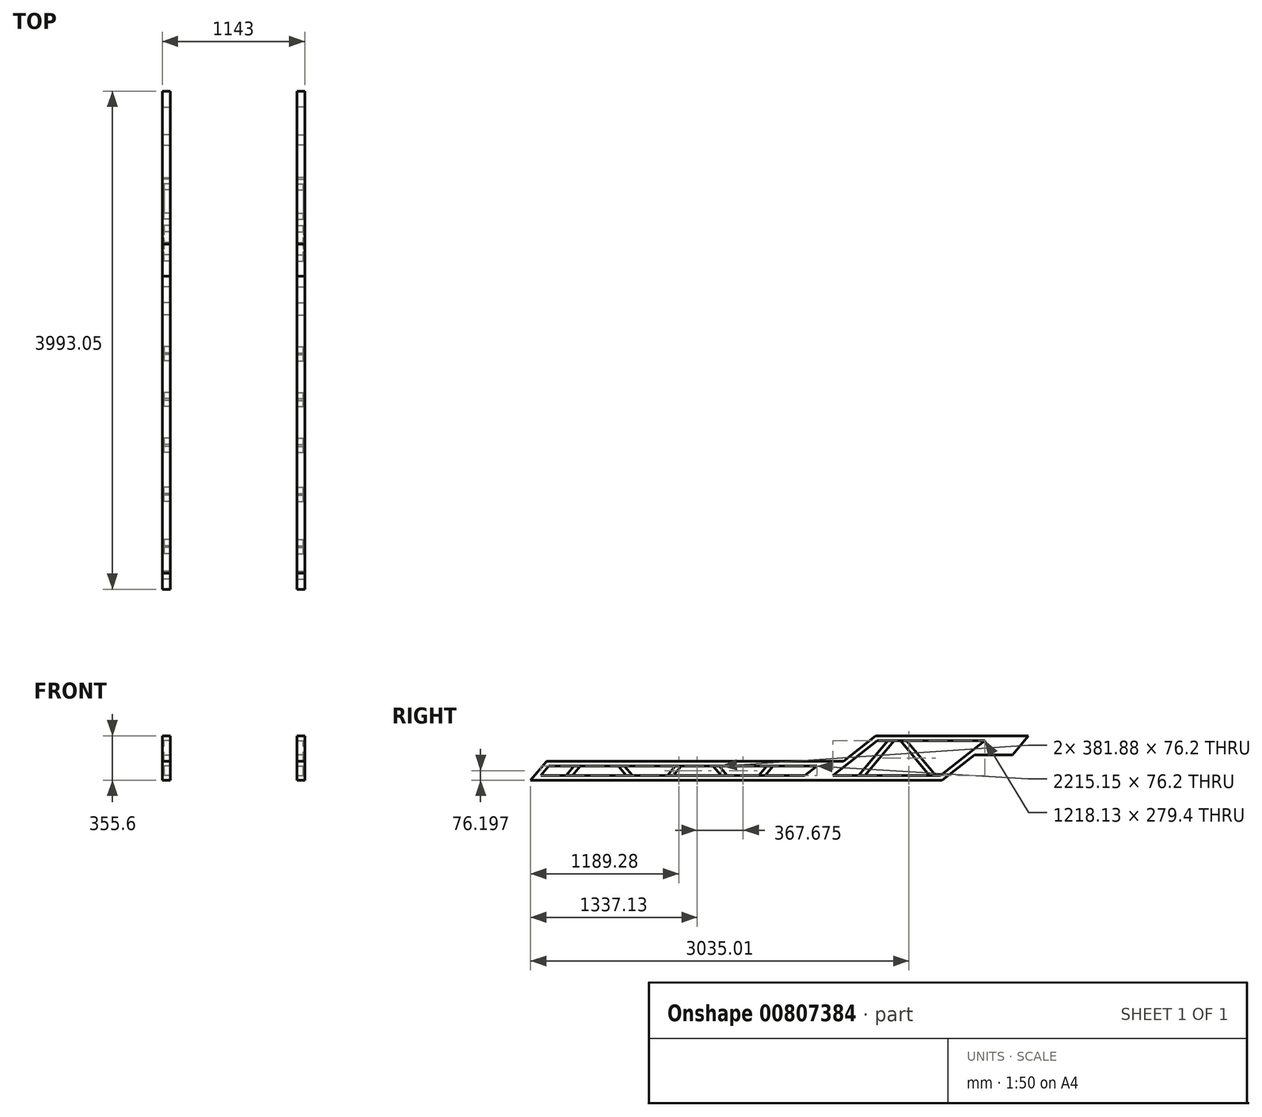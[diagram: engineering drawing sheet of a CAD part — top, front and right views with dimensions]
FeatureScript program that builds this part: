
annotation { "Feature Type Name" : "Feature", "Feature Type Description" : "" }
export const myFeature = defineFeature(function(context is Context, id is Id, definition is map)
    precondition{}
    {
        {
            var Q0;
            Q0=qCreatedBy(makeId("Right.planeOp"),FACE);
            var sketch = newSketch(context, id + "F0", { "sketchPlane" : qUnion([Q0])});
            skLineSegment(sketch, "E0", {"start": v(-1690.82, 358.4) * mm, "end": v(1611.18, 358.4) * mm});
            skLineSegment(sketch, "E1", {"start": v(-1690.82, 358.4) * mm, "end": v(-1562.95, 510.8) * mm});
            skLineSegment(sketch, "E2", {"start": v(-1562.95, 510.8) * mm, "end": v(818.83, 510.8) * mm});
            skLineSegment(sketch, "E3", {"start": v(818.83, 510.8) * mm, "end": v(1077.21, 714) * mm});
            skLineSegment(sketch, "E4", {"start": v(1077.21, 714) * mm, "end": v(2302.23, 714) * mm});
            skLineSegment(sketch, "E5", {"start": v(2302.23, 714) * mm, "end": v(2174.35, 561.6) * mm});
            skLineSegment(sketch, "E6", {"start": v(2174.35, 561.6) * mm, "end": v(1869.55, 561.6) * mm});
            skLineSegment(sketch, "E7", {"start": v(1869.55, 561.6) * mm, "end": v(1611.18, 358.4) * mm});
            skSolve(sketch);
        }
        {
            var Q0;
            Q0=makeQuery(id+"F0.imprint","IMPRINT",FACE,{"disambiguationData":[TD([[makeQuery(id+"F0.imprint","IMPRINT",EDGE,{"derivedFrom":sQuery(id+"F0.wireOp",EDGE,"E0")}),1.0]])]});
            extrude(context, id + "F1", {"entities" : qUnion([Q0]), "depth" : 63.5 * mm, "offsetDistance" : 25.4 * mm});
        }
        {
            var Q0;
            Q0=makeQuery(id+"F1.opExtrude","CAP_FACE",FACE,{"disambiguationData":[OSD([sQuery(id+"F0.wireOp",EDGE,"E0"),sQuery(id+"F0.wireOp",EDGE,"E1"),sQuery(id+"F0.wireOp",EDGE,"E2"),sQuery(id+"F0.wireOp",EDGE,"E3"),sQuery(id+"F0.wireOp",EDGE,"E4"),sQuery(id+"F0.wireOp",EDGE,"E5"),sQuery(id+"F0.wireOp",EDGE,"E6"),sQuery(id+"F0.wireOp",EDGE,"E7")])],"isStart":false});
            var sketch = newSketch(context, id + "F2", { "sketchPlane" : qUnion([Q0])});
            skLineSegment(sketch, "E8.0", {"start": v(832.02, 472.7) * mm, "end": v(1090.4, 675.9) * mm});
            skLineSegment(sketch, "E8.1", {"start": v(-1545.18, 472.7) * mm, "end": v(606.03, 472.7) * mm});
            skLineSegment(sketch, "E8.2", {"start": v(1090.4, 675.9) * mm, "end": v(1953.26, 675.9) * mm});
            skLineSegment(sketch, "E8.3", {"start": v(-1609.12, 396.5) * mm, "end": v(-1545.18, 472.7) * mm});
            skLineSegment(sketch, "E8.7", {"start": v(-1609.12, 396.5) * mm, "end": v(509.14, 396.5) * mm});
            skLineSegment(sketch, "E9", {"start": v(832.02, 472.7) * mm, "end": v(735.13, 396.5) * mm});
            skLineSegment(sketch, "E10", {"start": v(606.03, 472.7) * mm, "end": v(509.14, 396.5) * mm});
            skLineSegment(sketch, "E11.trimOffspring", {"start": v(735.13, 396.5) * mm, "end": v(1597.99, 396.5) * mm});
            skLineSegment(sketch, "E12", {"start": v(1597.99, 396.5) * mm, "end": v(1953.26, 675.9) * mm});
            skSolve(sketch);
        }
        {
            var Q0;
            Q0=makeQuery(id+"F2.imprint","IMPRINT",FACE,{"disambiguationData":[TD([[makeQuery(id+"F2.imprint","IMPRINT",EDGE,{"derivedFrom":sQuery(id+"F2.wireOp",EDGE,"E8.0")}),-1.0]])]});
            var Q1;
            Q1=makeQuery(id+"F2.imprint","IMPRINT",FACE,{"disambiguationData":[TD([[makeQuery(id+"F2.imprint","IMPRINT",EDGE,{"derivedFrom":sQuery(id+"F2.wireOp",EDGE,"E8.1")}),-1.0]])]});
            extrude(context, id + "F3", {"entities" : qUnion([Q0, Q1]), "operationType" : NewBodyOperationType.REMOVE, "oppositeDirection" : true, "depth" : 12.7 * mm, "offsetDistance" : 25.4 * mm});
        }
        {
            var Q0;
            Q0=makeQuery(id+"F3.boolean.opBoolean","COPY",FACE,{"derivedFrom":makeQuery(id+"F3.opExtrude","CAP_FACE",FACE,{"disambiguationData":[OSD([sQuery(id+"F2.wireOp",EDGE,"E8.0"),sQuery(id+"F2.wireOp",EDGE,"E8.1"),sQuery(id+"F2.wireOp",EDGE,"E8.2"),sQuery(id+"F2.wireOp",EDGE,"E8.3"),sQuery(id+"F2.wireOp",EDGE,"E8.4"),sQuery(id+"F2.wireOp",EDGE,"E8.5"),sQuery(id+"F2.wireOp",EDGE,"E8.6"),sQuery(id+"F2.wireOp",EDGE,"E8.7")])],"isStart":false})});
            var sketch = newSketch(context, id + "F4", { "sketchPlane" : qUnion([Q0])});
            skLineSegment(sketch, "E13", {"start": v(-1545.18, 472.7) * mm, "end": v(-1609.12, 396.5) * mm});
            skLineSegment(sketch, "E14", {"start": v(-987.44, 472.7) * mm, "end": v(-923.5, 396.5) * mm});
            skLineSegment(sketch, "E15", {"start": v(-937.7, 472.7) * mm, "end": v(-873.77, 396.5) * mm});
            skLineSegment(sketch, "E16", {"start": v(-594.37, 396.5) * mm, "end": v(-530.43, 472.7) * mm});
            skLineSegment(sketch, "E17", {"start": v(-480.7, 472.7) * mm, "end": v(-544.63, 396.5) * mm});
            skLineSegment(sketch, "E18.0", {"start": v(-1545.18, 472.7) * mm, "end": v(606.03, 472.7) * mm});
            skLineSegment(sketch, "E19.0", {"start": v(-1609.12, 396.5) * mm, "end": v(509.14, 396.5) * mm});
            skLineSegment(sketch, "E20.0.0", {"start": v(1611.18, 358.4) * mm, "end": v(1869.55, 561.6) * mm});
            skLineSegment(sketch, "E20.0.1", {"start": v(1869.55, 561.6) * mm, "end": v(2174.35, 561.6) * mm});
            skLineSegment(sketch, "E20.0.2", {"start": v(2174.35, 561.6) * mm, "end": v(2302.23, 714) * mm});
            skLineSegment(sketch, "E20.0.3", {"start": v(2302.23, 714) * mm, "end": v(1077.21, 714) * mm});
            skLineSegment(sketch, "E20.0.4", {"start": v(1077.21, 714) * mm, "end": v(818.83, 510.8) * mm});
            skLineSegment(sketch, "E20.0.5", {"start": v(818.83, 510.8) * mm, "end": v(-1562.95, 510.8) * mm});
            skLineSegment(sketch, "E20.0.6", {"start": v(-1562.95, 510.8) * mm, "end": v(-1690.82, 358.4) * mm});
            skLineSegment(sketch, "E20.0.7", {"start": v(-1690.82, 358.4) * mm, "end": v(1611.18, 358.4) * mm});
            skLineSegment(sketch, "E21", {"start": v(-1341.98, 472.7) * mm, "end": v(-1405.92, 396.5) * mm});
            skLineSegment(sketch, "E22", {"start": v(-1292.24, 472.7) * mm, "end": v(-1356.18, 396.5) * mm});
            skLineSegment(sketch, "E23", {"start": v(-226.7, 472.7) * mm, "end": v(-162.75, 396.5) * mm});
            skLineSegment(sketch, "E24", {"start": v(-113.02, 396.5) * mm, "end": v(-176.96, 472.7) * mm});
            skLineSegment(sketch, "E25", {"start": v(204.92, 472.7) * mm, "end": v(140.98, 396.5) * mm});
            skLineSegment(sketch, "E26", {"start": v(254.66, 472.7) * mm, "end": v(190.72, 396.5) * mm});
            skLineSegment(sketch, "E27", {"start": v(940.73, 396.5) * mm, "end": v(1175.17, 675.9) * mm});
            skLineSegment(sketch, "E28", {"start": v(1224.9, 675.9) * mm, "end": v(990.46, 396.5) * mm});
            skLineSegment(sketch, "E29", {"start": v(1510.15, 396.5) * mm, "end": v(1275.7, 675.9) * mm});
            skLineSegment(sketch, "E30", {"start": v(1559.89, 396.5) * mm, "end": v(1325.44, 675.9) * mm});
            skLineSegment(sketch, "E31.0", {"start": v(735.13, 396.5) * mm, "end": v(1090.4, 675.9) * mm});
            skLineSegment(sketch, "E32.0", {"start": v(735.13, 396.5) * mm, "end": v(1597.99, 396.5) * mm});
            skLineSegment(sketch, "E33.0", {"start": v(1090.4, 675.9) * mm, "end": v(1953.26, 675.9) * mm});
            skLineSegment(sketch, "E34.0", {"start": v(1597.99, 396.5) * mm, "end": v(1953.26, 675.9) * mm});
            skSolve(sketch);
        }
        {
            var Q0;
            {var subQ0=sQuery(id+"F4.wireOp",EDGE,"E27");Q0=makeQuery(id+"F4.imprint","IMPRINT",FACE,{"disambiguationData":[TD([[makeQuery(id+"F4.imprint","IMPRINT",EDGE,{"derivedFrom":subQ0}),1.0]])]});}
            var Q1;
            {var subQ0=sQuery(id+"F4.wireOp",EDGE,"E28");Q1=makeQuery(id+"F4.imprint","IMPRINT",FACE,{"disambiguationData":[TD([[makeQuery(id+"F4.imprint","IMPRINT",EDGE,{"derivedFrom":subQ0}),1.0]])]});}
            var Q2;
            {var subQ0=sQuery(id+"F4.wireOp",EDGE,"E30");Q2=makeQuery(id+"F4.imprint","IMPRINT",FACE,{"disambiguationData":[TD([[makeQuery(id+"F4.imprint","IMPRINT",EDGE,{"derivedFrom":subQ0}),-1.0]])]});}
            var Q3;
            {var subQ2=sQuery(id+"F4.wireOp",EDGE,"E26");Q3=makeQuery(id+"F4.imprint","IMPRINT",FACE,{"disambiguationData":[TD([[makeQuery(id+"F4.imprint","IMPRINT",EDGE,{"derivedFrom":subQ2}),1.0]])]});}
            var Q4;
            {var subQ0=sQuery(id+"F4.wireOp",EDGE,"E24");Q4=makeQuery(id+"F4.imprint","IMPRINT",FACE,{"disambiguationData":[TD([[makeQuery(id+"F4.imprint","IMPRINT",EDGE,{"derivedFrom":subQ0}),-1.0]])]});}
            var Q5;
            {var subQ0=sQuery(id+"F4.wireOp",EDGE,"E17");Q5=makeQuery(id+"F4.imprint","IMPRINT",FACE,{"disambiguationData":[TD([[makeQuery(id+"F4.imprint","IMPRINT",EDGE,{"derivedFrom":subQ0}),1.0]])]});}
            var Q6;
            {var subQ0=sQuery(id+"F4.wireOp",EDGE,"E13");Q6=makeQuery(id+"F4.imprint","IMPRINT",FACE,{"disambiguationData":[TD([[makeQuery(id+"F4.imprint","IMPRINT",EDGE,{"derivedFrom":subQ0}),-1.0]])]});}
            var Q7;
            {var subQ0=sQuery(id+"F4.wireOp",EDGE,"E14");Q7=makeQuery(id+"F4.imprint","IMPRINT",FACE,{"disambiguationData":[TD([[makeQuery(id+"F4.imprint","IMPRINT",EDGE,{"derivedFrom":subQ0}),-1.0]])]});}
            var Q8;
            {var subQ0=sQuery(id+"F4.wireOp",EDGE,"E15");Q8=makeQuery(id+"F4.imprint","IMPRINT",FACE,{"disambiguationData":[TD([[makeQuery(id+"F4.imprint","IMPRINT",EDGE,{"derivedFrom":subQ0}),1.0]])]});}
            var Q9;
            Q9=makeQuery(id+"F1.opExtrude","CAP_FACE",FACE,{"disambiguationData":[OSD([sQuery(id+"F0.wireOp",EDGE,"E0"),sQuery(id+"F0.wireOp",EDGE,"E1"),sQuery(id+"F0.wireOp",EDGE,"E2"),sQuery(id+"F0.wireOp",EDGE,"E3"),sQuery(id+"F0.wireOp",EDGE,"E4"),sQuery(id+"F0.wireOp",EDGE,"E5"),sQuery(id+"F0.wireOp",EDGE,"E6"),sQuery(id+"F0.wireOp",EDGE,"E7")])],"isStart":true});
            extrude(context, id + "F5", {"entities" : qUnion([Q0, Q1, Q2, Q3, Q4, Q5, Q6, Q7, Q8]), "operationType" : NewBodyOperationType.REMOVE, "endBound" : BoundingType.UP_TO_SURFACE, "oppositeDirection" : true, "depth" : 144.78 * mm, "endBoundEntityFace" : qUnion([Q9]), "offsetDistance" : 25.4 * mm});
        }
        {
            var Q0;
            Q0=qCreatedBy(makeId("Right.planeOp"),FACE);
            cPlane(context, id + "F6", {"entities" : qUnion([Q0]), "cplaneType" : CPlaneType.OFFSET, "offset" : 508 * mm, "oppositeDirection" : true, "width" : 152.4 * mm, "height" : 152.4 * mm});
        }
        {
            var Q0;
            Q0=makeQuery(id+"F1.opExtrude","SWEPT_BODY",BODY,{"disambiguationData":[OSD([sQuery(id+"F0.wireOp",EDGE,"E0"),sQuery(id+"F0.wireOp",EDGE,"E1"),sQuery(id+"F0.wireOp",EDGE,"E2"),sQuery(id+"F0.wireOp",EDGE,"E3"),sQuery(id+"F0.wireOp",EDGE,"E4"),sQuery(id+"F0.wireOp",EDGE,"E5"),sQuery(id+"F0.wireOp",EDGE,"E6"),sQuery(id+"F0.wireOp",EDGE,"E7")])]});
            var Q1;
            Q1=qCreatedBy(id+"F6.planeOp",FACE);
            mirror(context, id + "F7", {"entities" : qUnion([Q0]), "mirrorPlane" : qUnion([Q1])});
        }
    });
